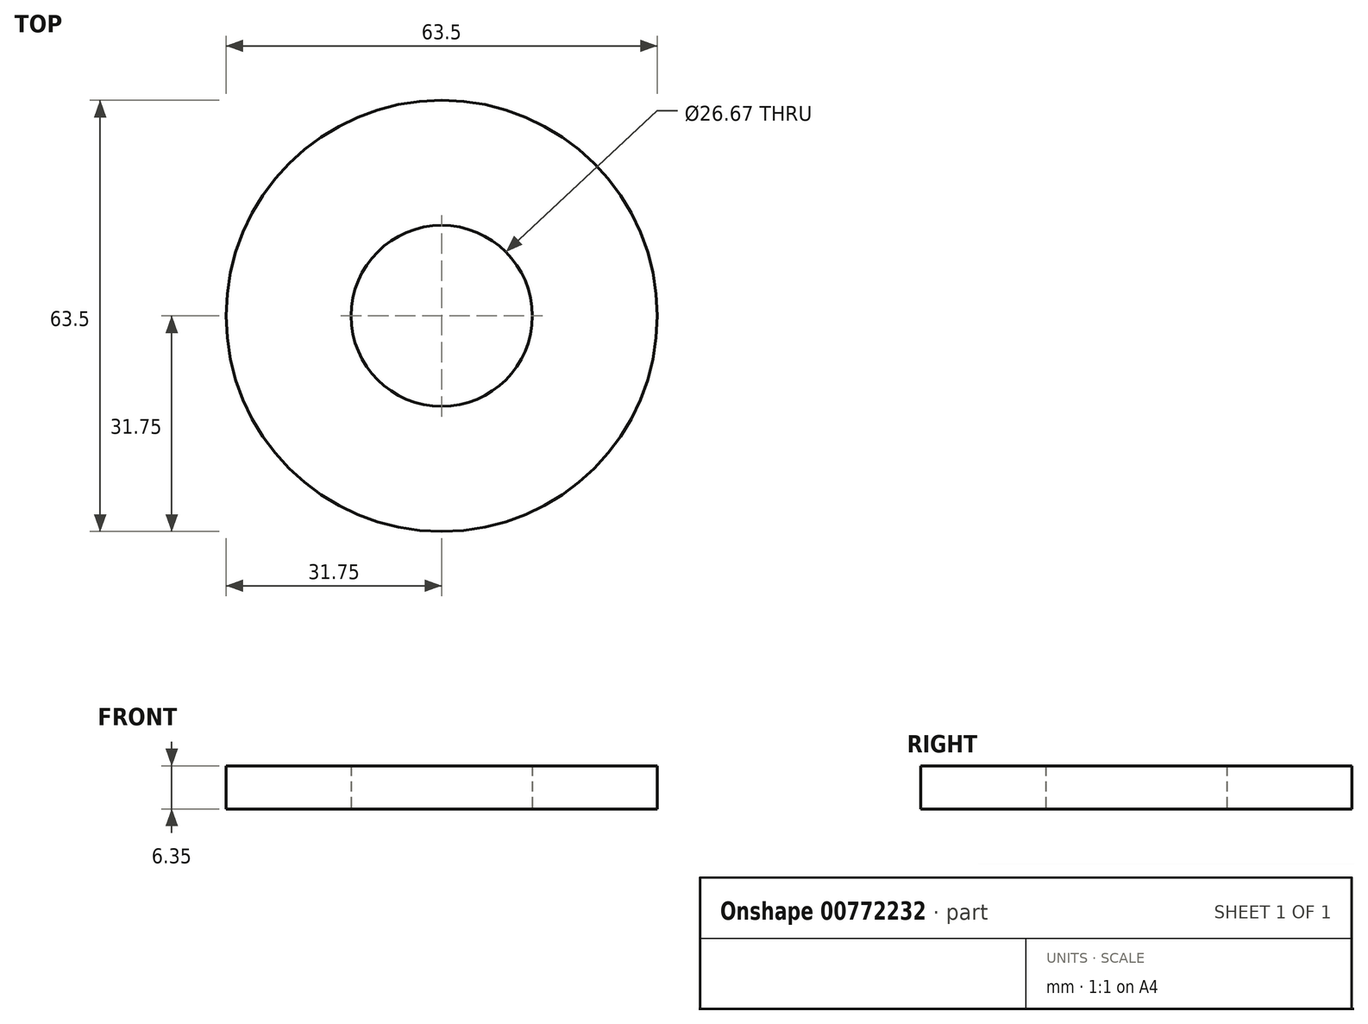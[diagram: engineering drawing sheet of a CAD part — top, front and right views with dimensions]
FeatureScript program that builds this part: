
annotation { "Feature Type Name" : "Feature", "Feature Type Description" : "" }
export const myFeature = defineFeature(function(context is Context, id is Id, definition is map)
    precondition{}
    {
        {
            var Q0;
            Q0=qCreatedBy(makeId("Top.planeOp"),FACE);
            var sketch = newSketch(context, id + "F0", { "sketchPlane" : qUnion([Q0])});
            skCircle(sketch, "E0", {"center": v(0, 0) * mm, "radius": 31.75 * mm});
            skCircle(sketch, "E1", {"center": v(0, 0) * mm, "radius": 13.34 * mm});
            skSolve(sketch);
        }
        {
            var Q0;
            Q0 = qSketchRegion(id + "F0", true);
            extrude(context, id + "F1", {"entities" : qUnion([Q0]), "depth" : 6.35 * mm, "offsetDistance" : 25.4 * mm});
        }
    });
